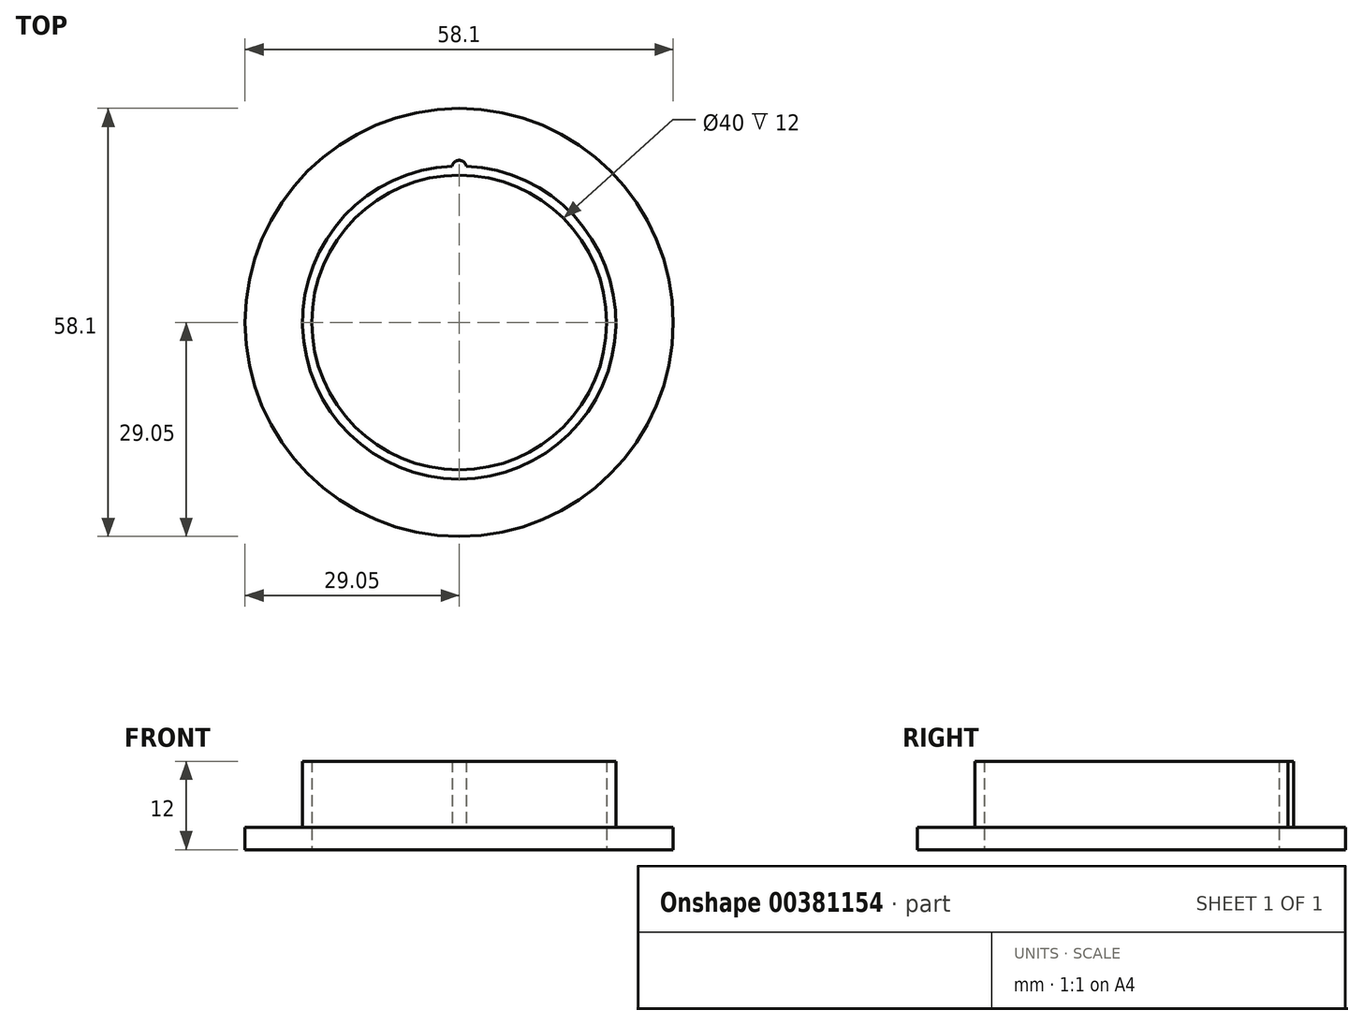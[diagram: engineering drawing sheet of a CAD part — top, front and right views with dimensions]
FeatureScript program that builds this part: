
annotation { "Feature Type Name" : "Feature", "Feature Type Description" : "" }
export const myFeature = defineFeature(function(context is Context, id is Id, definition is map)
    precondition{}
    {
        {
            var Q0;
            Q0=qCreatedBy(makeId("Front.planeOp"),FACE);
            var sketch = newSketch(context, id + "F0", { "sketchPlane" : qUnion([Q0])});
            skLineSegment(sketch, "E0", {"start": v(20, 0) * mm, "end": v(20, 12) * mm});
            skLineSegment(sketch, "E1", {"start": v(20, 12) * mm, "end": v(21.25, 12) * mm});
            skLineSegment(sketch, "E2", {"start": v(21.25, 12) * mm, "end": v(21.25, 3) * mm});
            skLineSegment(sketch, "E3", {"start": v(21.25, 3) * mm, "end": v(29.05, 3) * mm});
            skLineSegment(sketch, "E4", {"start": v(29.05, 3) * mm, "end": v(29.05, 0) * mm});
            skLineSegment(sketch, "E5", {"start": v(29.05, 0) * mm, "end": v(20, 0) * mm});
            skLineSegment(sketch, "E6", {"start": v(0, 0) * mm, "end": v(0, 14.53) * mm, "construction": true});
            skSolve(sketch);
        }
        {
            var Q0;
            Q0 = qSketchRegion(id + "F0", true);
            var Q1;
            Q1=sQuery(id+"F0.wireOp",EDGE,"E6");
            revolve(context, id + "F1", {"surfaceOperationType" : NewSurfaceOperationType.NEW, "entities" : qUnion([Q0]), "axis" : qUnion([Q1]), "revolveType" : RevolveType.FULL});
        }
        {
            var Q0;
            Q0=makeQuery(id+"F1.opRevolve","SWEPT_FACE",FACE,{"disambiguationData":[OSD([sQuery(id+"F0.wireOp",EDGE,"E3")])]});
            var sketch = newSketch(context, id + "F2", { "sketchPlane" : qUnion([Q0])});
            skArc(sketch, "E7", {"start": v(0.97, 21.23) * mm, "mid": v(0, 22) * mm, "end": v(-0.97, 21.23) * mm});
            skArc(sketch, "E8.0", {"start": v(0.97, 21.23) * mm, "mid": v(0, 21.25) * mm, "end": v(-0.97, 21.23) * mm});
            skSolve(sketch);
        }
        {
            var Q0;
            Q0 = qSketchRegion(id + "F2", true);
            var Q1;
            Q1=makeQuery(id+"F1.opRevolve","SWEPT_FACE",FACE,{"disambiguationData":[OSD([sQuery(id+"F0.wireOp",EDGE,"E1")])]});
            extrude(context, id + "F3", {"entities" : qUnion([Q0]), "operationType" : NewBodyOperationType.ADD, "endBound" : BoundingType.UP_TO_SURFACE, "depth" : 25 * mm, "endBoundEntityFace" : qUnion([Q1]), "offsetDistance" : 25 * mm});
        }
    });
